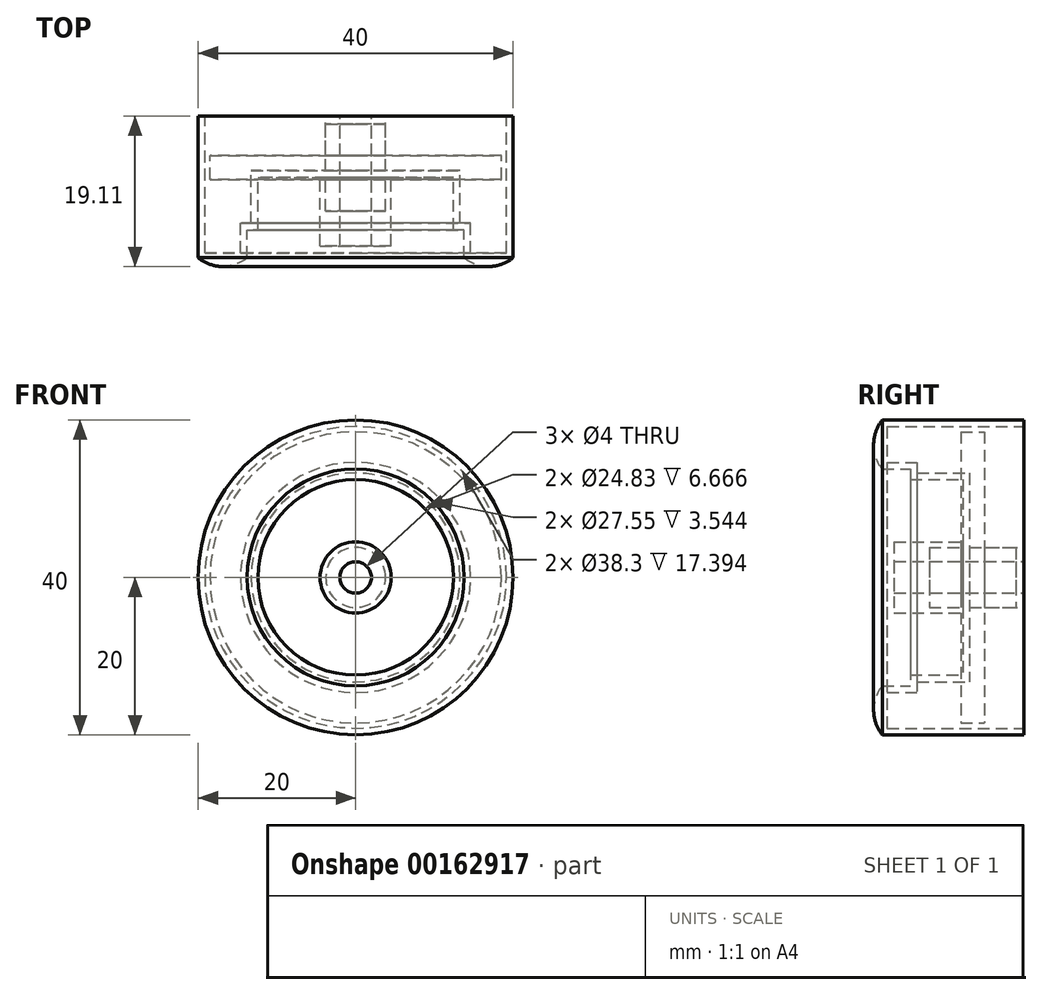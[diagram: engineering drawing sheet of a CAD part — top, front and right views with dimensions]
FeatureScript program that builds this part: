
annotation { "Feature Type Name" : "Feature", "Feature Type Description" : "" }
export const myFeature = defineFeature(function(context is Context, id is Id, definition is map)
    precondition{}
    {
        {
            var Q0;
            Q0=qCreatedBy(makeId("Top.planeOp"),FACE);
            var sketch = newSketch(context, id + "F0", { "sketchPlane" : qUnion([Q0])});
            skLineSegment(sketch, "E0", {"start": v(0, 17.4) * mm, "end": v(0, -20.43) * mm, "construction": true});
            skLineSegment(sketch, "E1", {"start": v(2, 6.54) * mm, "end": v(2, -9.96) * mm});
            skLineSegment(sketch, "E2", {"start": v(2, -9.96) * mm, "end": v(4.51, -9.96) * mm});
            skLineSegment(sketch, "E3", {"start": v(4.51, -9.96) * mm, "end": v(4.51, -1.25) * mm});
            skLineSegment(sketch, "E4", {"start": v(4.51, -1.25) * mm, "end": v(12.42, -1.25) * mm});
            skLineSegment(sketch, "E5", {"start": v(12.42, -1.25) * mm, "end": v(12.42, -7.92) * mm});
            skLineSegment(sketch, "E6", {"start": v(12.42, -7.92) * mm, "end": v(13.78, -7.92) * mm});
            skLineSegment(sketch, "E7", {"start": v(13.78, -7.92) * mm, "end": v(13.78, -11.46) * mm});
            skLineSegment(sketch, "E8", {"start": v(20, -11.46) * mm, "end": v(20, 6.54) * mm});
            skLineSegment(sketch, "E9.0", {"start": v(19.15, -10.86) * mm, "end": v(19.15, 6.54) * mm});
            skLineSegment(sketch, "E9.1", {"start": v(14.62, -10.86) * mm, "end": v(19.15, -10.86) * mm});
            skLineSegment(sketch, "E9.2", {"start": v(14.62, -7.07) * mm, "end": v(14.62, -10.86) * mm});
            skLineSegment(sketch, "E9.3", {"start": v(13.27, -7.07) * mm, "end": v(14.62, -7.07) * mm});
            skLineSegment(sketch, "E9.4", {"start": v(13.27, -0.4) * mm, "end": v(13.27, -7.07) * mm});
            skLineSegment(sketch, "E9.8", {"start": v(3.8, -0.4) * mm, "end": v(13.27, -0.4) * mm});
            skLineSegment(sketch, "E10", {"start": v(19.15, 6.54) * mm, "end": v(20, 6.54) * mm});
            skLineSegment(sketch, "E11", {"start": v(2, 6.54) * mm, "end": v(3.8, 6.54) * mm});
            skLineSegment(sketch, "E12", {"start": v(3.8, 6.54) * mm, "end": v(3.8, -0.4) * mm});
            skArc(sketch, "E13", {"start": v(13.78, -11.46) * mm, "mid": v(16.89, -12.57) * mm, "end": v(20, -11.46) * mm});
            skLineSegment(sketch, "E14", {"start": v(16.89, -10.86) * mm, "end": v(16.89, -7.65) * mm, "construction": true});
            skSolve(sketch);
        }
        {
            var Q0;
            Q0=makeQuery(id+"F0.imprint","IMPRINT",FACE,{"disambiguationData":[TD([[makeQuery(id+"F0.imprint","IMPRINT",EDGE,{"derivedFrom":sQuery(id+"F0.wireOp",EDGE,"E1")}),1.0]])]});
            var Q1;
            Q1=sQuery(id+"F0.wireOp",EDGE,"E0");
            revolve(context, id + "F1", {"entities" : qUnion([Q0]), "axis" : qUnion([Q1]), "revolveType" : RevolveType.FULL});
        }
        {
            var Q0;
            Q0=qCreatedBy(makeId("Top.planeOp"),FACE);
            var sketch = newSketch(context, id + "F2", { "sketchPlane" : qUnion([Q0])});
            skLineSegment(sketch, "E15.0", {"start": v(0, 17.4) * mm, "end": v(0, -20.43) * mm, "construction": true});
            skLineSegment(sketch, "E16.0", {"start": v(2, 5.5) * mm, "end": v(2, -5.5) * mm});
            skLineSegment(sketch, "E17", {"start": v(3.8, 5.5) * mm, "end": v(3.8, 1.5) * mm});
            skLineSegment(sketch, "E18", {"start": v(3.8, 1.5) * mm, "end": v(18.5, 1.5) * mm});
            skLineSegment(sketch, "E19", {"start": v(18.5, 1.5) * mm, "end": v(18.5, -1.5) * mm});
            skLineSegment(sketch, "E20", {"start": v(18.5, -1.5) * mm, "end": v(3.8, -1.5) * mm});
            skLineSegment(sketch, "E21", {"start": v(3.8, -1.5) * mm, "end": v(3.8, -5.5) * mm});
            skLineSegment(sketch, "E22", {"start": v(2, -5.5) * mm, "end": v(3.8, -5.5) * mm});
            skLineSegment(sketch, "E23", {"start": v(0, 0) * mm, "end": v(6.69, 0) * mm, "construction": true});
            skLineSegment(sketch, "E24", {"start": v(2, 5.5) * mm, "end": v(3.8, 5.5) * mm});
            skSolve(sketch);
        }
        {
            var Q0;
            Q0 = qSketchRegion(id + "F0", true);
            var Q1;
            Q1=sQuery(id+"F2.wireOp",EDGE,"E15.0");
            revolve(context, id + "F3", {"entities" : qUnion([Q0]), "axis" : qUnion([Q1]), "revolveType" : RevolveType.FULL});
        }
        {
            var Q0;
            Q0 = qSketchRegion(id + "F2", true);
            var Q1;
            Q1=sQuery(id+"F2.wireOp",EDGE,"E15.0");
            revolve(context, id + "F4", {"entities" : qUnion([Q0]), "axis" : qUnion([Q1]), "revolveType" : RevolveType.FULL});
        }
    });
